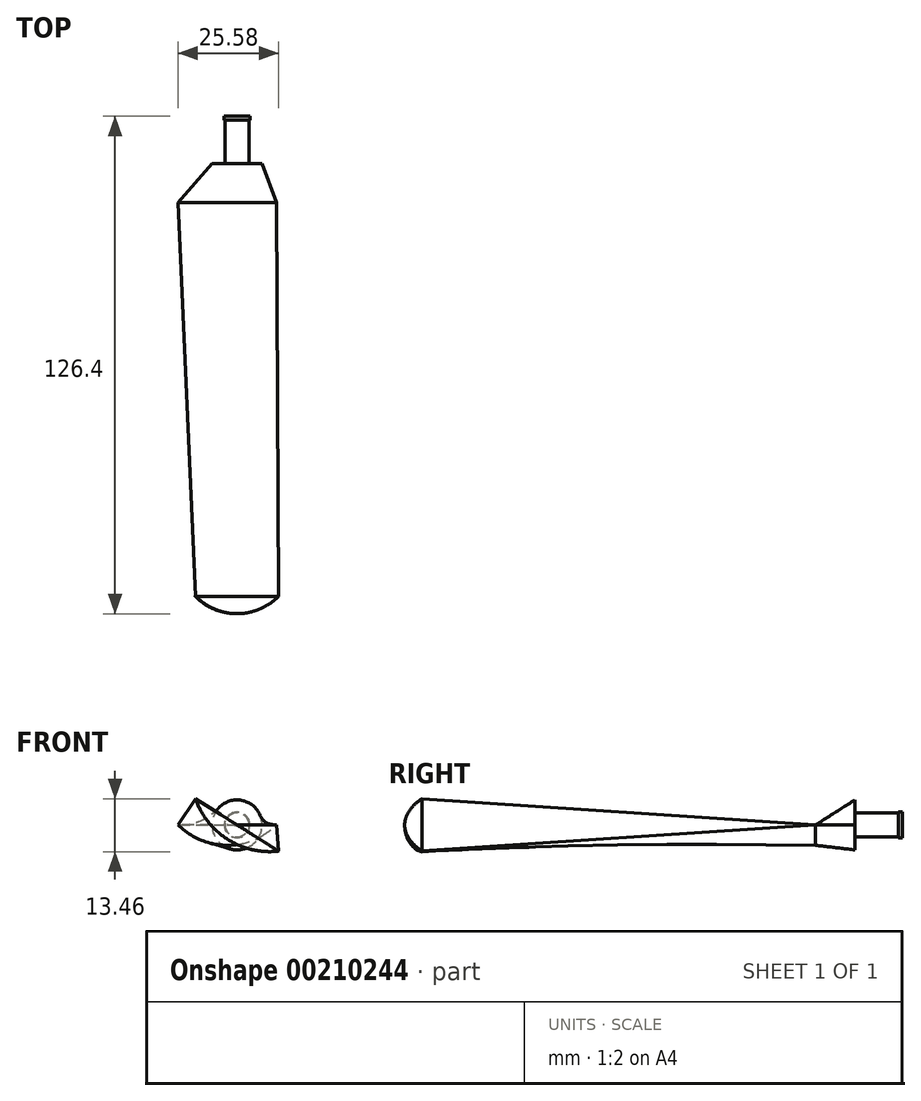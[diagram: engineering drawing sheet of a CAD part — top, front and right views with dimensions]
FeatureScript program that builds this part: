
annotation { "Feature Type Name" : "Feature", "Feature Type Description" : "" }
export const myFeature = defineFeature(function(context is Context, id is Id, definition is map)
    precondition{}
    {
        {
            var Q0;
            Q0=qCreatedBy(makeId("Front.planeOp"),FACE);
            var sketch = newSketch(context, id + "F0", { "sketchPlane" : qUnion([Q0])});
            skCircle(sketch, "E0", {"center": v(0, 0) * mm, "radius": 6.35 * mm});
            skSolve(sketch);
        }
        {
            var Q0;
            Q0=qCreatedBy(makeId("Front.planeOp"),FACE);
            cPlane(context, id + "F1", {"entities" : qUnion([Q0]), "cplaneType" : CPlaneType.OFFSET, "offset" : 10 * mm, "width" : 152.4 * mm, "height" : 152.4 * mm});
        }
        {
            var Q0;
            Q0=qCreatedBy(id+"F1.planeOp",FACE);
            cPlane(context, id + "F2", {"entities" : qUnion([Q0]), "cplaneType" : CPlaneType.OFFSET, "offset" : 100 * mm, "width" : 152.4 * mm, "height" : 152.4 * mm});
        }
        {
            var Q0;
            Q0=qCreatedBy(id+"F1.planeOp",FACE);
            var sketch = newSketch(context, id + "F3", { "sketchPlane" : qUnion([Q0])});
            skLineSegment(sketch, "E1", {"start": v(0, 0) * mm, "end": v(10, 0) * mm, "construction": true});
            skLineSegment(sketch, "E2", {"start": v(0, 0) * mm, "end": v(-15, 0) * mm, "construction": true});
            skLineSegment(sketch, "E3", {"start": v(0, 0) * mm, "end": v(0, 12.7) * mm, "construction": true});
            skLineSegment(sketch, "E4", {"start": v(0, 0) * mm, "end": v(0, -5) * mm, "construction": true});
            skArc(sketch, "E5", {"start": v(-15, 0) * mm, "mid": v(-2.5, -5.18) * mm, "end": v(10, 0) * mm});
            skLineSegment(sketch, "E6", {"start": v(-15, 0) * mm, "end": v(10, 0) * mm});
            skSolve(sketch);
        }
        {
            var Q0;
            Q0=qCreatedBy(id+"F2.planeOp",FACE);
            var sketch = newSketch(context, id + "F4", { "sketchPlane" : qUnion([Q0])});
            skLineSegment(sketch, "E7", {"start": v(0, 0) * mm, "end": v(12.7, 0) * mm, "construction": true});
            skLineSegment(sketch, "E8", {"start": v(0, 0) * mm, "end": v(-12.7, 0) * mm, "construction": true});
            skLineSegment(sketch, "E9", {"start": v(-12.7, 0) * mm, "end": v(-12.7, 8) * mm, "construction": true});
            skLineSegment(sketch, "E10", {"start": v(12.7, 0) * mm, "end": v(12.7, -8) * mm, "construction": true});
            skLineSegment(sketch, "E11", {"start": v(-12.7, 8) * mm, "end": v(12.7, -8) * mm, "construction": true});
            skLineSegment(sketch, "E12", {"start": v(0, 0) * mm, "end": v(-10.58, 6.66) * mm, "construction": true});
            skLineSegment(sketch, "E13", {"start": v(0, 0) * mm, "end": v(10.58, -6.66) * mm, "construction": true});
            skLineSegment(sketch, "E14", {"start": v(-10.58, 6.66) * mm, "end": v(10.58, -6.66) * mm});
            skArc(sketch, "E15", {"start": v(-10.58, 6.66) * mm, "mid": v(-2.34, -3.71) * mm, "end": v(10.58, -6.66) * mm});
            skSolve(sketch);
        }
        {
            var Q0;
            Q0=makeQuery(id+"F0.imprint","IMPRINT",FACE,{"disambiguationData":[TD([[makeQuery(id+"F0.imprint","IMPRINT",EDGE,{"derivedFrom":sQuery(id+"F0.wireOp",EDGE,"E0")}),1.0]])]});
            var Q1;
            Q1=makeQuery(id+"F3.imprint","IMPRINT",FACE,{"disambiguationData":[TD([[makeQuery(id+"F3.imprint","IMPRINT",EDGE,{"derivedFrom":sQuery(id+"F3.wireOp",EDGE,"E5")}),1.0]])]});
            loft(context, id + "F5", {"sheetProfilesArray" : [{ "sheetProfileEntities" : qUnion([Q0]) }, { "sheetProfileEntities" : qUnion([Q1]) }]});
        }
        {
            var Q1;
            Q1=makeQuery(id+"F3.imprint","IMPRINT",FACE,{"disambiguationData":[TD([[makeQuery(id+"F3.imprint","IMPRINT",EDGE,{"derivedFrom":sQuery(id+"F3.wireOp",EDGE,"E5")}),1.0]])]});
            var Q2;
            {var subQ0=sQuery(id+"F4.wireOp",EDGE,"E15");Q2=makeQuery(id+"F4.imprint","IMPRINT",FACE,{"disambiguationData":[TD([[makeQuery(id+"F4.imprint","IMPRINT",EDGE,{"derivedFrom":subQ0}),1.0]])]});}
            loft(context, id + "F6", {"operationType" : NewBodyOperationType.ADD, "sheetProfilesArray" : [{ "sheetProfileEntities" : qUnion([Q1]) }, { "sheetProfileEntities" : qUnion([Q2]) }]});
        }
        {
            var Q0;
            Q0=makeQuery(id+"F5.opLoft","CAP_FACE",FACE,{"disambiguationData":[OSD([makeQuery(id+"F0.imprint","IMPRINT",FACE,{"disambiguationData":[TD([[makeQuery(id+"F0.imprint","IMPRINT",EDGE,{"derivedFrom":sQuery(id+"F0.wireOp",EDGE,"E0")}),1.0]])]})])],"isStart":true});
            var sketch = newSketch(context, id + "F7", { "sketchPlane" : qUnion([Q0])});
            skCircle(sketch, "E16", {"center": v(0, 0) * mm, "radius": 3.05 * mm});
            skSolve(sketch);
        }
        {
            var Q0;
            Q0 = qSketchRegion(id + "F7", true);
            extrude(context, id + "F8", {"entities" : qUnion([Q0]), "operationType" : NewBodyOperationType.ADD, "depth" : 11 * mm});
        }
        {
            var Q0;
            Q0=makeQuery(id+"F6.opLoft","CAP_FACE",FACE,{"disambiguationData":[OSD([makeQuery(id+"F4.imprint","IMPRINT",FACE,{"disambiguationData":[TD([[makeQuery(id+"F4.imprint","IMPRINT",EDGE,{"derivedFrom":sQuery(id+"F4.wireOp",EDGE,"E14")}),-1.0]])]})])],"isStart":true});
            var sketch = newSketch(context, id + "F9", { "sketchPlane" : qUnion([Q0])});
            skLineSegment(sketch, "E17.0.0", {"start": v(10.58, -6.66) * mm, "end": v(-10.58, 6.66) * mm});
            skFitSpline(sketch, "E17.0.1", {"points": [v(-10.58, 6.66) * mm, v(-10.4, 6.13) * mm, v(-10.19, 5.6) * mm, v(-9.96, 5.1) * mm, v(-9.73, 4.58) * mm, v(-9.48, 4.07) * mm, v(-9.2, 3.58) * mm, v(-8.94, 3.09) * mm, v(-8.65, 2.6) * mm, v(-8.33, 2.14) * mm, v(-8.02, 1.67) * mm, v(-7.7, 1.21) * mm, v(-7.34, 0.77) * mm, v(-7, 0.33) * mm, v(-6.62, -0.1) * mm, v(-6.24, -0.5) * mm, v(-5.85, -0.91) * mm, v(-5.45, -1.3) * mm, v(-5.03, -1.68) * mm, v(-4.61, -2.06) * mm, v(-4.18, -2.41) * mm, v(-3.73, -2.75) * mm, v(-3.28, -3.1) * mm, v(-2.82, -3.41) * mm, v(-2.34, -3.71) * mm, v(-1.86, -4.01) * mm, v(-1.37, -4.3) * mm, v(-0.87, -4.55) * mm, v(-0.37, -4.8) * mm, v(0.14, -5.05) * mm, v(0.66, -5.26) * mm, v(1.18, -5.48) * mm, v(1.7, -5.67) * mm, v(2.24, -5.84) * mm, v(2.78, -6.01) * mm, v(3.32, -6.16) * mm, v(3.87, -6.29) * mm, v(4.42, -6.41) * mm, v(4.97, -6.52) * mm, v(5.53, -6.6) * mm, v(6.08, -6.67) * mm, v(6.64, -6.73) * mm, v(7.2, -6.76) * mm, v(7.77, -6.8) * mm, v(8.33, -6.8) * mm, v(8.9, -6.78) * mm, v(9.46, -6.77) * mm, v(10.02, -6.73) * mm, v(10.58, -6.66) * mm]});
            skArc(sketch, "E18", {"start": v(-10.58, 6.66) * mm, "mid": v(-2.34, -3.71) * mm, "end": v(10.58, -6.66) * mm});
            skPoint(sketch, "E19", {"position": v(-2.34, -3.71) * mm});
            skSolve(sketch);
        }
        {
            var Q0;
            Q0 = qSketchRegion(id + "F9", true);
            var Q1;
            Q1=sQuery(id+"F9.wireOp",EDGE,"E17.0.0");
            revolve(context, id + "F10", {"entities" : qUnion([Q0]), "axis" : qUnion([Q1]), "revolveType" : RevolveType.ONE_DIRECTION, "angle" : 90 * degree});
        }
        {
            var Q0;
            Q0 = qSketchRegion(id + "F7", true);
            extrude(context, id + "F11", {"entities" : qUnion([Q0]), "operationType" : NewBodyOperationType.ADD, "depth" : 8 * mm});
        }
        {
            var Q0;
            Q0=makeQuery(id+"F8.opExtrude","CAP_FACE",FACE,{"disambiguationData":[OSD([sQuery(id+"F7.wireOp",EDGE,"E16")])],"isStart":false});
            var sketch = newSketch(context, id + "F12", { "sketchPlane" : qUnion([Q0])});
            skCircle(sketch, "E20", {"center": v(0, 0) * mm, "radius": 3.25 * mm});
            skSolve(sketch);
        }
        {
            var Q0;
            Q0 = qSketchRegion(id + "F12", true);
            extrude(context, id + "F13", {"entities" : qUnion([Q0]), "operationType" : NewBodyOperationType.ADD, "depth" : 1 * mm});
        }
    });
